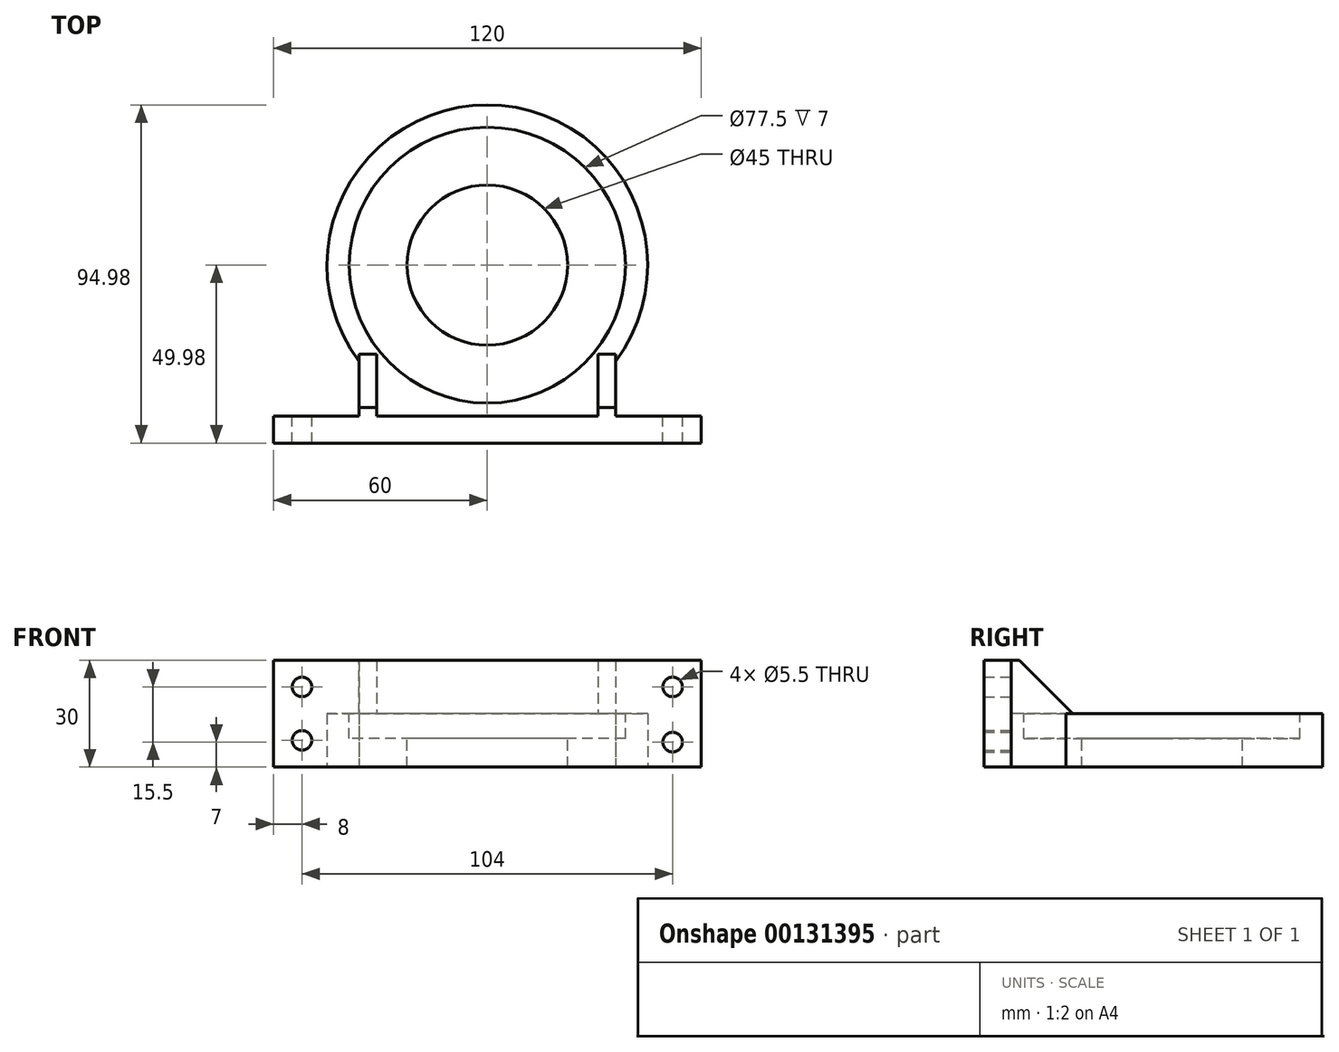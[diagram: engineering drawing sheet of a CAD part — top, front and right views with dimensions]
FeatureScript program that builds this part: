
annotation { "Feature Type Name" : "Feature", "Feature Type Description" : "" }
export const myFeature = defineFeature(function(context is Context, id is Id, definition is map)
    precondition{}
    {
        {
            var Q0;
            Q0=qCreatedBy(makeId("Top.planeOp"),FACE);
            var sketch = newSketch(context, id + "F0", { "sketchPlane" : qUnion([Q0])});
            skCircle(sketch, "E0", {"center": v(0, 0) * mm, "radius": 45 * mm});
            skLineSegment(sketch, "E1.bottom", {"start": v(-36, -27) * mm, "end": v(36, -27) * mm});
            skLineSegment(sketch, "E1.top", {"start": v(-36, -50) * mm, "end": v(36, -50) * mm});
            skLineSegment(sketch, "E1.left", {"start": v(-36, -27) * mm, "end": v(-36, -50) * mm});
            skLineSegment(sketch, "E1.right", {"start": v(36, -27) * mm, "end": v(36, -50) * mm});
            skLineSegment(sketch, "E2.bottom", {"start": v(-60, -42.37) * mm, "end": v(60, -42.37) * mm});
            skLineSegment(sketch, "E2.top", {"start": v(-60, -49.98) * mm, "end": v(60, -49.98) * mm});
            skLineSegment(sketch, "E2.left", {"start": v(-60, -42.37) * mm, "end": v(-60, -49.98) * mm});
            skLineSegment(sketch, "E2.right", {"start": v(60, -42.37) * mm, "end": v(60, -49.98) * mm});
            skSolve(sketch);
        }
        {
            var Q0;
            {var subQ0=sQuery(id+"F0.wireOp",EDGE,"E1.bottom");Q0=makeQuery(id+"F0.imprint","IMPRINT",FACE,{"disambiguationData":[TD([[makeQuery(id+"F0.imprint","IMPRINT",EDGE,{"derivedFrom":subQ0}),1.0]])]});}
            var Q1;
            {var subQ0=sQuery(id+"F0.wireOp",EDGE,"E1.left");var subQ3=sQuery(id+"F0.wireOp",EDGE,"E2.bottom");var subQ5=makeQuery(id+"F0.imprint","INTERSECT",VERTEX,{"derivedFrom":[subQ0,subQ3]});Q1=makeQuery(id+"F0.imprint","IMPRINT",FACE,{"disambiguationData":[TD([[makeQuery(id+"F0.imprint","IMPRINT",EDGE,{"disambiguationData":[TD([[subQ5,-1.0]])],"derivedFrom":subQ3}),1.0]])]});}
            var Q2;
            {var subQ0=sQuery(id+"F0.wireOp",EDGE,"E1.bottom");Q2=makeQuery(id+"F0.imprint","IMPRINT",FACE,{"disambiguationData":[TD([[makeQuery(id+"F0.imprint","IMPRINT",EDGE,{"derivedFrom":subQ0}),-1.0]])]});}
            var Q3;
            {var subQ0=sQuery(id+"F0.wireOp",EDGE,"E2.bottom");var subQ1=sQuery(id+"F0.wireOp",EDGE,"E0");var subQ2=makeQuery(id+"F0.imprint","INTERSECT",VERTEX,{"disambiguationData":[OD(0.0)],"derivedFrom":[subQ1,subQ0]});Q3=makeQuery(id+"F0.imprint","IMPRINT",FACE,{"disambiguationData":[TD([[makeQuery(id+"F0.imprint","IMPRINT",EDGE,{"disambiguationData":[TD([[subQ2,-1.0]])],"derivedFrom":subQ1}),1.0]])]});}
            var Q4;
            {var subQ5=sQuery(id+"F0.wireOp",EDGE,"E2.left");Q4=makeQuery(id+"F0.imprint","IMPRINT",FACE,{"disambiguationData":[TD([[makeQuery(id+"F0.imprint","IMPRINT",EDGE,{"derivedFrom":subQ5}),1.0]])]});}
            var Q5;
            {var subQ0=sQuery(id+"F0.wireOp",EDGE,"E2.bottom");var subQ3=sQuery(id+"F0.wireOp",EDGE,"E0");var subQ4=makeQuery(id+"F0.imprint","INTERSECT",VERTEX,{"disambiguationData":[OD(0.0)],"derivedFrom":[subQ3,subQ0]});Q5=makeQuery(id+"F0.imprint","IMPRINT",FACE,{"disambiguationData":[TD([[makeQuery(id+"F0.imprint","IMPRINT",EDGE,{"disambiguationData":[TD([[subQ4,-1.0]])],"derivedFrom":subQ3}),-1.0]])]});}
            var Q6;
            {var subQ5=sQuery(id+"F0.wireOp",EDGE,"E2.right");Q6=makeQuery(id+"F0.imprint","IMPRINT",FACE,{"disambiguationData":[TD([[makeQuery(id+"F0.imprint","IMPRINT",EDGE,{"derivedFrom":subQ5}),-1.0]])]});}
            var Q7;
            {var subQ0=sQuery(id+"F0.wireOp",EDGE,"E1.right");var subQ3=sQuery(id+"F0.wireOp",EDGE,"E2.bottom");var subQ5=makeQuery(id+"F0.imprint","INTERSECT",VERTEX,{"derivedFrom":[subQ0,subQ3]});Q7=makeQuery(id+"F0.imprint","IMPRINT",FACE,{"disambiguationData":[TD([[makeQuery(id+"F0.imprint","IMPRINT",EDGE,{"disambiguationData":[TD([[subQ5,1.0]])],"derivedFrom":subQ3}),1.0]])]});}
            extrude(context, id + "F1", {"entities" : qUnion([Q0, Q1, Q2, Q3, Q4, Q5, Q6, Q7]), "depth" : 15 * mm});
        }
        {
            var Q0;
            Q0=makeQuery(id+"F1.opExtrude","CAP_FACE",FACE,{"disambiguationData":[OSD([sQuery(id+"F0.wireOp",EDGE,"E0"),sQuery(id+"F0.wireOp",EDGE,"E1.left"),sQuery(id+"F0.wireOp",EDGE,"E1.right"),sQuery(id+"F0.wireOp",EDGE,"E2.bottom"),sQuery(id+"F0.wireOp",EDGE,"E2.top"),sQuery(id+"F0.wireOp",EDGE,"E2.left"),sQuery(id+"F0.wireOp",EDGE,"E2.right")])],"isStart":false});
            var sketch = newSketch(context, id + "F2", { "sketchPlane" : qUnion([Q0])});
            skCircle(sketch, "E3", {"center": v(0, 0) * mm, "radius": 38.75 * mm});
            skSolve(sketch);
        }
        {
            var Q0;
            Q0=makeQuery(id+"F1.opExtrude","CAP_FACE",FACE,{"disambiguationData":[OSD([sQuery(id+"F0.wireOp",EDGE,"E0"),sQuery(id+"F0.wireOp",EDGE,"E1.left"),sQuery(id+"F0.wireOp",EDGE,"E1.right"),sQuery(id+"F0.wireOp",EDGE,"E2.bottom"),sQuery(id+"F0.wireOp",EDGE,"E2.top"),sQuery(id+"F0.wireOp",EDGE,"E2.left"),sQuery(id+"F0.wireOp",EDGE,"E2.right")])],"isStart":false});
            var sketch = newSketch(context, id + "F3", { "sketchPlane" : qUnion([Q0])});
            skLineSegment(sketch, "E4.bottom", {"start": v(-60, -42.37) * mm, "end": v(60, -42.37) * mm});
            skLineSegment(sketch, "E4.top", {"start": v(-60, -49.98) * mm, "end": v(60, -49.98) * mm});
            skLineSegment(sketch, "E4.left", {"start": v(-60, -42.37) * mm, "end": v(-60, -49.98) * mm});
            skLineSegment(sketch, "E4.right", {"start": v(60, -42.37) * mm, "end": v(60, -49.98) * mm});
            skSolve(sketch);
        }
        {
            var Q0;
            Q0 = qSketchRegion(id + "F2", true);
            extrude(context, id + "F4", {"entities" : qUnion([Q0]), "operationType" : NewBodyOperationType.REMOVE, "oppositeDirection" : true, "depth" : 7 * mm});
        }
        {
            var Q0;
            Q0=makeQuery(id+"F3.imprint","IMPRINT",FACE,{"disambiguationData":[TD([[makeQuery(id+"F3.imprint","IMPRINT",EDGE,{"derivedFrom":sQuery(id+"F3.wireOp",EDGE,"E4.top")}),1.0]])]});
            extrude(context, id + "F5", {"entities" : qUnion([Q0]), "operationType" : NewBodyOperationType.ADD, "depth" : 15 * mm});
        }
        {
            var Q0;
            Q0=makeQuery(id+"F1.opExtrude","CAP_FACE",FACE,{"disambiguationData":[OSD([sQuery(id+"F0.wireOp",EDGE,"E0"),sQuery(id+"F0.wireOp",EDGE,"E1.left"),sQuery(id+"F0.wireOp",EDGE,"E1.right"),sQuery(id+"F0.wireOp",EDGE,"E2.bottom"),sQuery(id+"F0.wireOp",EDGE,"E2.top"),sQuery(id+"F0.wireOp",EDGE,"E2.left"),sQuery(id+"F0.wireOp",EDGE,"E2.right")])],"isStart":false});
            var sketch = newSketch(context, id + "F6", { "sketchPlane" : qUnion([Q0])});
            skLineSegment(sketch, "E5.bottom", {"start": v(-36, -25.03) * mm, "end": v(-31, -25.03) * mm});
            skLineSegment(sketch, "E5.top", {"start": v(-36, -42.53) * mm, "end": v(-31, -42.53) * mm});
            skLineSegment(sketch, "E5.left", {"start": v(-36, -25.03) * mm, "end": v(-36, -42.53) * mm});
            skLineSegment(sketch, "E5.right", {"start": v(-31, -25.03) * mm, "end": v(-31, -42.53) * mm});
            skLineSegment(sketch, "E6.bottom", {"start": v(31, -25.03) * mm, "end": v(36, -25.03) * mm});
            skLineSegment(sketch, "E6.top", {"start": v(31, -42.53) * mm, "end": v(36, -42.53) * mm});
            skLineSegment(sketch, "E6.left", {"start": v(31, -25.03) * mm, "end": v(31, -42.53) * mm});
            skLineSegment(sketch, "E6.right", {"start": v(36, -25.03) * mm, "end": v(36, -42.53) * mm});
            skSolve(sketch);
        }
        {
            var Q0;
            {var subQ0=sQuery(id+"F6.wireOp",EDGE,"E5.bottom");Q0=makeQuery(id+"F6.imprint","IMPRINT",FACE,{"disambiguationData":[TD([[makeQuery(id+"F6.imprint","IMPRINT",EDGE,{"derivedFrom":subQ0}),-1.0]])]});}
            var Q1;
            {var subQ0=sQuery(id+"F6.wireOp",EDGE,"E6.bottom");Q1=makeQuery(id+"F6.imprint","IMPRINT",FACE,{"disambiguationData":[TD([[makeQuery(id+"F6.imprint","IMPRINT",EDGE,{"derivedFrom":subQ0}),-1.0]])]});}
            extrude(context, id + "F7", {"entities" : qUnion([Q0, Q1]), "operationType" : NewBodyOperationType.ADD, "depth" : 15 * mm});
        }
        {
            var Q0;
            Q0=makeQuery(id+"F7.opExtrude","CAP_EDGE",EDGE,{"disambiguationData":[OSD([sQuery(id+"F6.wireOp",EDGE,"E5.bottom")])],"isStart":false});
            var Q1;
            Q1=makeQuery(id+"F7.opExtrude","CAP_EDGE",EDGE,{"disambiguationData":[OSD([sQuery(id+"F6.wireOp",EDGE,"E6.bottom")])],"isStart":false});
            chamfer(context, id + "F8", {"entities" : qUnion([Q0, Q1]), "width" : 15 * mm, "tangentPropagation" : true});
        }
        {
            var Q0;
            {var subQ0=sQuery(id+"F0.wireOp",EDGE,"E2.left");var subQ1=sQuery(id+"F0.wireOp",EDGE,"E2.right");var subQ3=sQuery(id+"F0.wireOp",EDGE,"E2.bottom");var subQ5=sQuery(id+"F0.wireOp",EDGE,"E1.left");var subQ9=sQuery(id+"F3.wireOp",EDGE,"E4.bottom");Q0=makeQuery(id+"F7.boolean.opBoolean","SPLIT",FACE,{"disambiguationData":[TD([makeQuery(id+"F1.opExtrude","SWEPT_FACE",FACE,{"disambiguationData":[OSD([subQ5])]})])],"derivedFrom":makeQuery(id+"F5.boolean.opBoolean","MERGE",FACE,{"derivedFrom":[makeQuery(id+"F1.opExtrude","SWEPT_FACE",FACE,{"disambiguationData":[OSD([subQ3]),TDD([makeQuery(id+"F0.imprint","IMPRINT",EDGE,{"disambiguationData":[TD([[makeQuery(id+"F0.imprint","INTERSECT",VERTEX,{"derivedFrom":[subQ3,subQ0]}),-1.0]])],"derivedFrom":subQ3})])]}),makeQuery(id+"F1.opExtrude","SWEPT_FACE",FACE,{"disambiguationData":[OSD([subQ3]),TDD([makeQuery(id+"F0.imprint","IMPRINT",EDGE,{"disambiguationData":[TD([[makeQuery(id+"F0.imprint","INTERSECT",VERTEX,{"derivedFrom":[subQ3,subQ1]}),1.0]])],"derivedFrom":subQ3})])]}),makeQuery(id+"F5.opExtrude","SWEPT_FACE",FACE,{"disambiguationData":[OSD([subQ9])]})]})});}
            var sketch = newSketch(context, id + "F9", { "sketchPlane" : qUnion([Q0])});
            skCircle(sketch, "E7", {"center": v(52, 7.5) * mm, "radius": 2.75 * mm});
            skCircle(sketch, "E8", {"center": v(52, 22.5) * mm, "radius": 2.75 * mm});
            skCircle(sketch, "E9", {"center": v(-52, 7) * mm, "radius": 2.75 * mm});
            skCircle(sketch, "E10", {"center": v(-52, 22.5) * mm, "radius": 2.75 * mm});
            skSolve(sketch);
        }
        {
            var Q0;
            Q0=makeQuery(id+"F9.imprint","IMPRINT",FACE,{"disambiguationData":[TD([[makeQuery(id+"F9.imprint","IMPRINT",EDGE,{"derivedFrom":sQuery(id+"F9.wireOp",EDGE,"E7")}),1.0]])]});
            var Q1;
            Q1=makeQuery(id+"F9.imprint","IMPRINT",FACE,{"disambiguationData":[TD([[makeQuery(id+"F9.imprint","IMPRINT",EDGE,{"derivedFrom":sQuery(id+"F9.wireOp",EDGE,"E8")}),1.0]])]});
            var Q2;
            Q2=makeQuery(id+"F9.imprint","IMPRINT",FACE,{"disambiguationData":[TD([[makeQuery(id+"F9.imprint","IMPRINT",EDGE,{"derivedFrom":sQuery(id+"F9.wireOp",EDGE,"E9")}),1.0]])]});
            var Q3;
            Q3=makeQuery(id+"F9.imprint","IMPRINT",FACE,{"disambiguationData":[TD([[makeQuery(id+"F9.imprint","IMPRINT",EDGE,{"derivedFrom":sQuery(id+"F9.wireOp",EDGE,"E10")}),1.0]])]});
            extrude(context, id + "F10", {"entities" : qUnion([Q0, Q1, Q2, Q3]), "operationType" : NewBodyOperationType.REMOVE, "oppositeDirection" : true, "depth" : 25 * mm});
        }
        {
            var Q0;
            Q0=makeQuery(id+"F4.boolean.opBoolean","COPY",FACE,{"derivedFrom":makeQuery(id+"F4.opExtrude","CAP_FACE",FACE,{"disambiguationData":[OSD([sQuery(id+"F2.wireOp",EDGE,"E3")])],"isStart":false})});
            var sketch = newSketch(context, id + "F11", { "sketchPlane" : qUnion([Q0])});
            skCircle(sketch, "E11", {"center": v(0, 0) * mm, "radius": 22.5 * mm});
            skSolve(sketch);
        }
        {
            var Q0;
            Q0=makeQuery(id+"F11.imprint","IMPRINT",FACE,{"disambiguationData":[TD([[makeQuery(id+"F11.imprint","IMPRINT",EDGE,{"derivedFrom":sQuery(id+"F11.wireOp",EDGE,"E11")}),1.0]])]});
            extrude(context, id + "F12", {"entities" : qUnion([Q0]), "operationType" : NewBodyOperationType.REMOVE, "oppositeDirection" : true, "depth" : 25 * mm});
        }
    });
